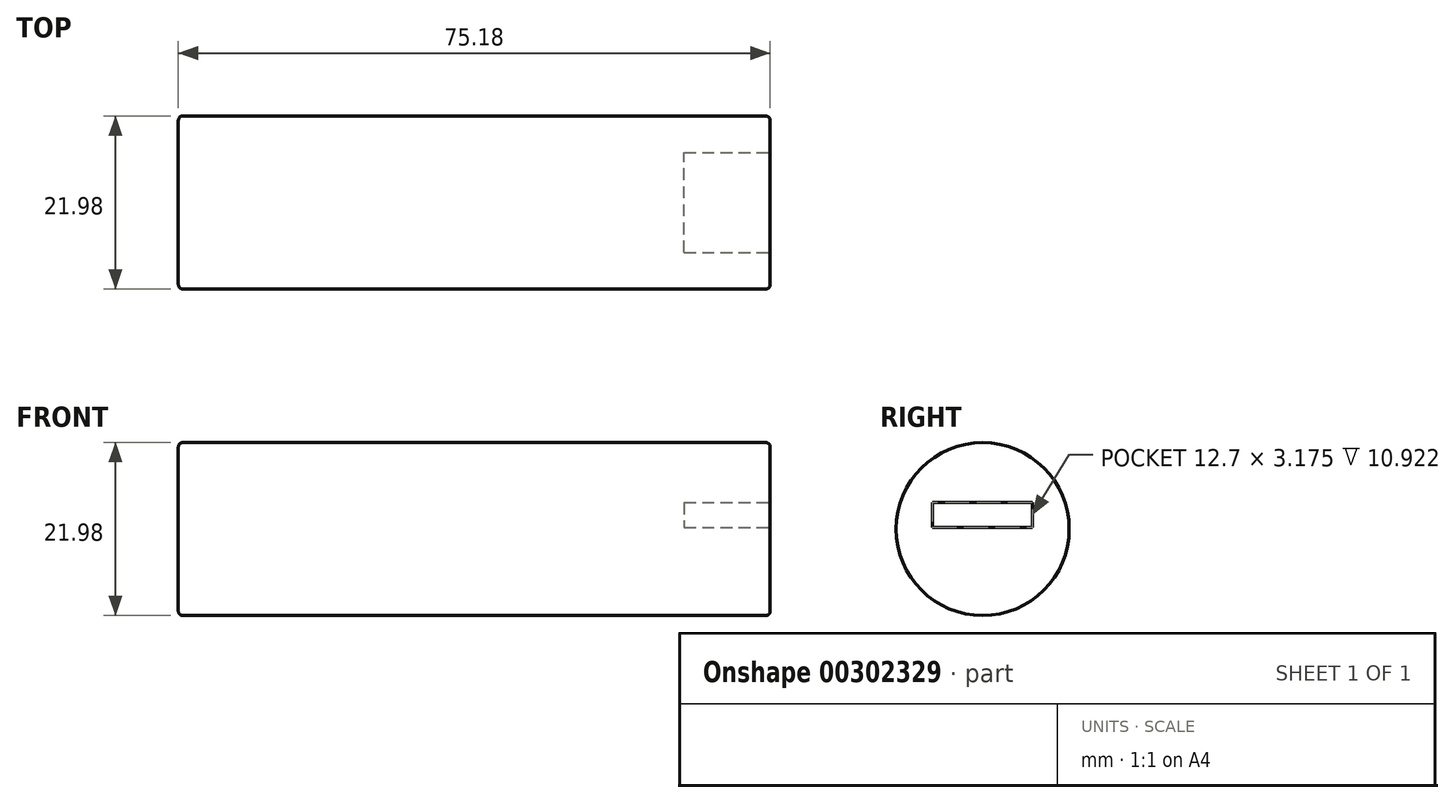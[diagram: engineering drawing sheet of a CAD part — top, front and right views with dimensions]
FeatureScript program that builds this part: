
annotation { "Feature Type Name" : "Feature", "Feature Type Description" : "" }
export const myFeature = defineFeature(function(context is Context, id is Id, definition is map)
    precondition{}
    {
        {
            var Q0;
            Q0=qCreatedBy(makeId("Right.planeOp"),FACE);
            var sketch = newSketch(context, id + "F0", { "sketchPlane" : qUnion([Q0])});
            skCircle(sketch, "E0", {"center": v(0, 0) * mm, "radius": 10.99 * mm});
            skSolve(sketch);
        }
        {
            var Q0;
            Q0 = qSketchRegion(id + "F0", true);
            extrude(context, id + "F1", {"entities" : qUnion([Q0]), "depth" : 75.18 * mm, "symmetric" : true});
        }
        {
            var Q0;
            Q0=makeQuery(id+"F1.opExtrude","CAP_FACE",FACE,{"disambiguationData":[OSD([sQuery(id+"F0.wireOp",EDGE,"E0")])],"isStart":false});
            var sketch = newSketch(context, id + "F2", { "sketchPlane" : qUnion([Q0])});
            skLineSegment(sketch, "E1.bottom", {"start": v(-6.35, 3.37) * mm, "end": v(6.35, 3.37) * mm});
            skLineSegment(sketch, "E1.top", {"start": v(-6.35, 0.2) * mm, "end": v(6.35, 0.2) * mm});
            skLineSegment(sketch, "E1.left", {"start": v(-6.35, 3.37) * mm, "end": v(-6.35, 0.2) * mm});
            skLineSegment(sketch, "E1.right", {"start": v(6.35, 3.37) * mm, "end": v(6.35, 0.2) * mm});
            skLineSegment(sketch, "E2", {"start": v(0, 0) * mm, "end": v(0, 0.2) * mm, "construction": true});
            skSolve(sketch);
        }
        {
            var Q0;
            Q0 = qSketchRegion(id + "F2", true);
            extrude(context, id + "F3", {"entities" : qUnion([Q0]), "operationType" : NewBodyOperationType.REMOVE, "oppositeDirection" : true, "depth" : 10.92 * mm});
        }
        {
            var Q0;
            Q0=makeQuery(id+"F1.opExtrude","CAP_EDGE",EDGE,{"disambiguationData":[OSD([sQuery(id+"F0.wireOp",EDGE,"E0")])],"isStart":false});
            var Q1;
            Q1=makeQuery(id+"F1.opExtrude","CAP_EDGE",EDGE,{"disambiguationData":[OSD([sQuery(id+"F0.wireOp",EDGE,"E0")])],"isStart":true});
            fillet(context, id + "F4", {"entities" : qUnion([Q0, Q1]), "radius" : 0.55 * mm, "tangentPropagation" : true, "allowEdgeOverflow" : false});
        }
    });
